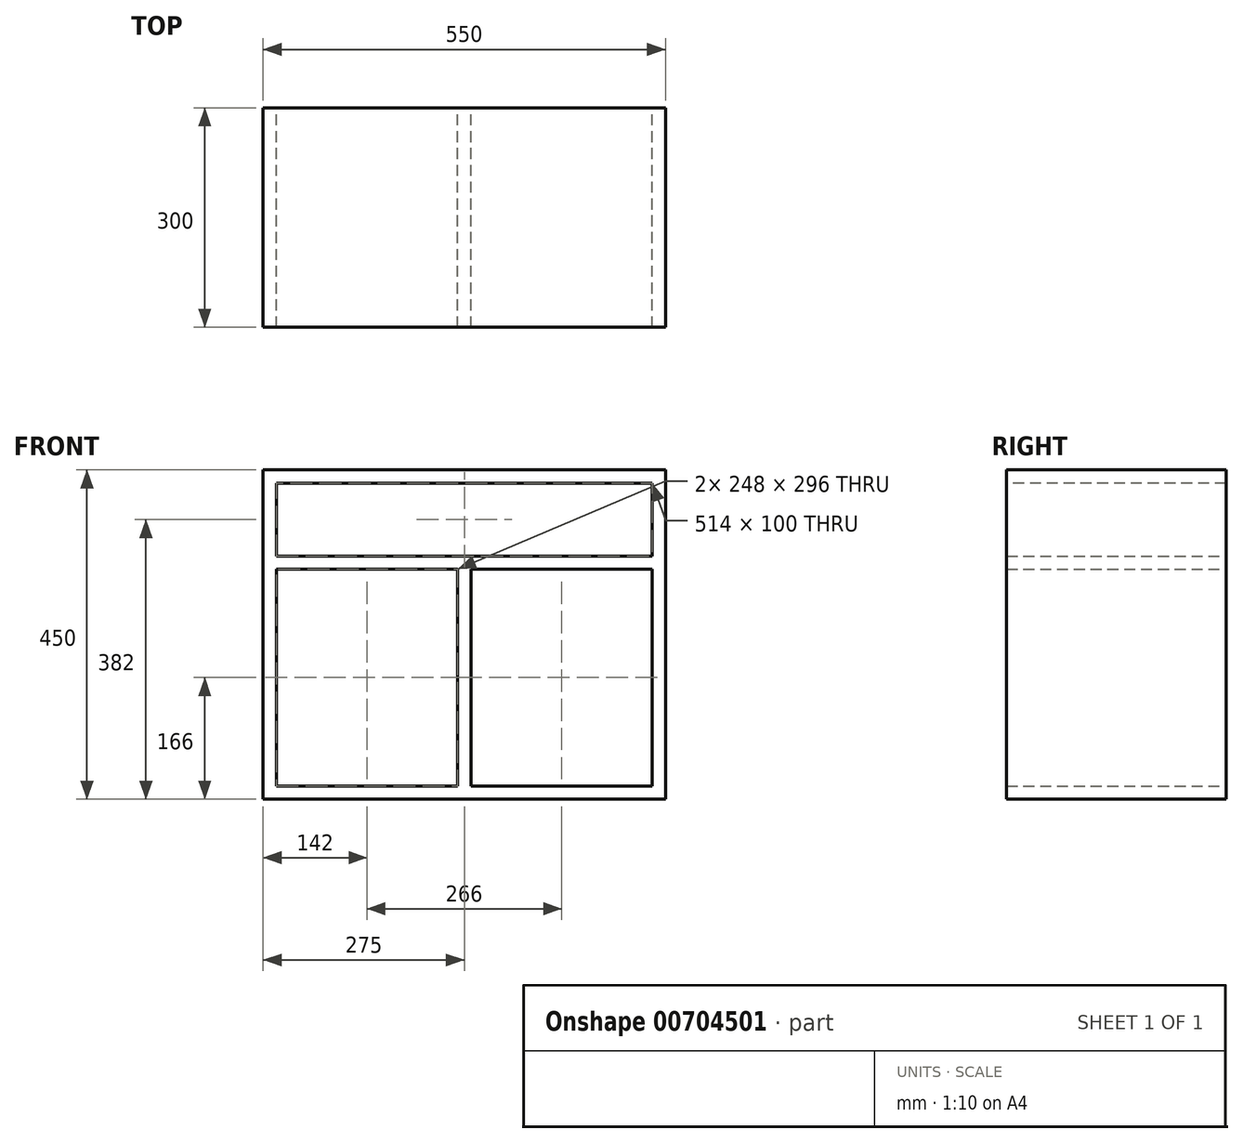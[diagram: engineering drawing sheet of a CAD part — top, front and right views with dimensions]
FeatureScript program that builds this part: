
annotation { "Feature Type Name" : "Feature", "Feature Type Description" : "" }
export const myFeature = defineFeature(function(context is Context, id is Id, definition is map)
    precondition{}
    {
        {
            var Q0;
            Q0=qCreatedBy(makeId("Top.planeOp"),FACE);
            var sketch = newSketch(context, id + "F0", { "sketchPlane" : qUnion([Q0])});
            skLineSegment(sketch, "E0.bottom", {"start": v(275, -150) * mm, "end": v(-275, -150) * mm});
            skLineSegment(sketch, "E0.top", {"start": v(275, 150) * mm, "end": v(-275, 150) * mm});
            skLineSegment(sketch, "E0.left", {"start": v(275, -150) * mm, "end": v(275, 150) * mm});
            skLineSegment(sketch, "E0.right", {"start": v(-275, -150) * mm, "end": v(-275, 150) * mm});
            skPoint(sketch, "E0.middle", {"position": v(0, 0) * mm});
            skSolve(sketch);
        }
        {
            var Q0;
            Q0=makeQuery(id+"F0.imprint","IMPRINT",FACE,{"disambiguationData":[TD([[makeQuery(id+"F0.imprint","IMPRINT",EDGE,{"derivedFrom":sQuery(id+"F0.wireOp",EDGE,"E0.bottom")}),-1.0]])]});
            extrude(context, id + "F1", {"entities" : qUnion([Q0]), "depth" : 18 * mm, "offsetDistance" : 25 * mm});
        }
        {
            var Q0;
            Q0=makeQuery(id+"F1.opExtrude","CAP_FACE",FACE,{"disambiguationData":[OSD([sQuery(id+"F0.wireOp",EDGE,"E0.bottom"),sQuery(id+"F0.wireOp",EDGE,"E0.top"),sQuery(id+"F0.wireOp",EDGE,"E0.left"),sQuery(id+"F0.wireOp",EDGE,"E0.right")])],"isStart":false});
            var sketch = newSketch(context, id + "F2", { "sketchPlane" : qUnion([Q0])});
            skLineSegment(sketch, "E1.bottom", {"start": v(-275, 150) * mm, "end": v(-257, 150) * mm});
            skLineSegment(sketch, "E1.top", {"start": v(-275, -150) * mm, "end": v(-257, -150) * mm});
            skLineSegment(sketch, "E1.left", {"start": v(-275, 150) * mm, "end": v(-275, -150) * mm});
            skLineSegment(sketch, "E1.right", {"start": v(-257, 150) * mm, "end": v(-257, -150) * mm});
            skLineSegment(sketch, "E2.bottom", {"start": v(257, 150) * mm, "end": v(275, 150) * mm});
            skLineSegment(sketch, "E2.top", {"start": v(257, -150) * mm, "end": v(275, -150) * mm});
            skLineSegment(sketch, "E2.left", {"start": v(257, 150) * mm, "end": v(257, -150) * mm});
            skLineSegment(sketch, "E2.right", {"start": v(275, 150) * mm, "end": v(275, -150) * mm});
            skSolve(sketch);
        }
        {
            var Q0;
            Q0 = qSketchRegion(id + "F2", true);
            extrude(context, id + "F3", {"entities" : qUnion([Q0]), "operationType" : NewBodyOperationType.ADD, "depth" : 414 * mm, "offsetDistance" : 25 * mm});
        }
        {
            var Q0;
            Q0=makeQuery(id+"F1.opExtrude","CAP_FACE",FACE,{"disambiguationData":[OSD([sQuery(id+"F0.wireOp",EDGE,"E0.bottom"),sQuery(id+"F0.wireOp",EDGE,"E0.top"),sQuery(id+"F0.wireOp",EDGE,"E0.left"),sQuery(id+"F0.wireOp",EDGE,"E0.right")])],"isStart":false});
            var sketch = newSketch(context, id + "F4", { "sketchPlane" : qUnion([Q0])});
            skLineSegment(sketch, "E3.bottom", {"start": v(9, -150) * mm, "end": v(-9, -150) * mm});
            skLineSegment(sketch, "E3.top", {"start": v(9, 150) * mm, "end": v(-9, 150) * mm});
            skLineSegment(sketch, "E3.left", {"start": v(9, -150) * mm, "end": v(9, 150) * mm});
            skLineSegment(sketch, "E3.right", {"start": v(-9, -150) * mm, "end": v(-9, 150) * mm});
            skPoint(sketch, "E3.middle", {"position": v(0, 0) * mm});
            skSolve(sketch);
        }
        {
            var Q0;
            Q0 = qSketchRegion(id + "F4", true);
            extrude(context, id + "F5", {"entities" : qUnion([Q0]), "operationType" : NewBodyOperationType.ADD, "depth" : 296 * mm, "offsetDistance" : 25 * mm});
        }
        {
            var Q0;
            Q0=makeQuery(id+"F5.opExtrude","CAP_FACE",FACE,{"disambiguationData":[OSD([sQuery(id+"F4.wireOp",EDGE,"E3.bottom"),sQuery(id+"F4.wireOp",EDGE,"E3.top"),sQuery(id+"F4.wireOp",EDGE,"E3.left"),sQuery(id+"F4.wireOp",EDGE,"E3.right")])],"isStart":false});
            var sketch = newSketch(context, id + "F6", { "sketchPlane" : qUnion([Q0])});
            skLineSegment(sketch, "E4.bottom", {"start": v(257, -150) * mm, "end": v(-257, -150) * mm});
            skLineSegment(sketch, "E4.top", {"start": v(257, 150) * mm, "end": v(-257, 150) * mm});
            skLineSegment(sketch, "E4.left", {"start": v(257, -150) * mm, "end": v(257, 150) * mm});
            skLineSegment(sketch, "E4.right", {"start": v(-257, -150) * mm, "end": v(-257, 150) * mm});
            skPoint(sketch, "E4.middle", {"position": v(0, 0) * mm});
            skSolve(sketch);
        }
        {
            var Q0;
            {var subQ2=sQuery(id+"F6.wireOp",EDGE,"E4.left");Q0=makeQuery(id+"F6.imprint","IMPRINT",FACE,{"disambiguationData":[TD([[makeQuery(id+"F6.imprint","IMPRINT",EDGE,{"derivedFrom":subQ2}),1.0]])]});}
            var Q1;
            {var subQ1=makeQuery(id+"F5.opExtrude","CAP_EDGE",EDGE,{"disambiguationData":[OSD([sQuery(id+"F4.wireOp",EDGE,"E3.left")])],"isStart":false});Q1=makeQuery(id+"F6.imprint","IMPRINT",FACE,{"disambiguationData":[TD([[makeQuery(id+"F6.imprint","IMPRINT",EDGE,{"derivedFrom":subQ1}),1.0]])]});}
            var Q2;
            {var subQ2=sQuery(id+"F6.wireOp",EDGE,"E4.right");Q2=makeQuery(id+"F6.imprint","IMPRINT",FACE,{"disambiguationData":[TD([[makeQuery(id+"F6.imprint","IMPRINT",EDGE,{"derivedFrom":subQ2}),-1.0]])]});}
            extrude(context, id + "F7", {"entities" : qUnion([Q0, Q1, Q2]), "operationType" : NewBodyOperationType.ADD, "depth" : 18 * mm, "offsetDistance" : 25 * mm});
        }
        {
            var Q0;
            Q0=makeQuery(id+"F3.opExtrude","CAP_FACE",FACE,{"disambiguationData":[OSD([sQuery(id+"F2.wireOp",EDGE,"E1.bottom"),sQuery(id+"F2.wireOp",EDGE,"E1.top"),sQuery(id+"F2.wireOp",EDGE,"E1.left"),sQuery(id+"F2.wireOp",EDGE,"E1.right")])],"isStart":false});
            var sketch = newSketch(context, id + "F8", { "sketchPlane" : qUnion([Q0])});
            skLineSegment(sketch, "E5.bottom", {"start": v(275, -150) * mm, "end": v(-275, -150) * mm});
            skLineSegment(sketch, "E5.top", {"start": v(275, 150) * mm, "end": v(-275, 150) * mm});
            skLineSegment(sketch, "E5.left", {"start": v(275, -150) * mm, "end": v(275, 150) * mm});
            skLineSegment(sketch, "E5.right", {"start": v(-275, -150) * mm, "end": v(-275, 150) * mm});
            skPoint(sketch, "E5.middle", {"position": v(0, 0) * mm});
            skSolve(sketch);
        }
        {
            var Q0;
            {var subQ2=sQuery(id+"F8.wireOp",EDGE,"E5.left");Q0=makeQuery(id+"F8.imprint","IMPRINT",FACE,{"disambiguationData":[TD([[makeQuery(id+"F8.imprint","IMPRINT",EDGE,{"derivedFrom":subQ2}),1.0]])]});}
            var Q1;
            {var subQ0=sQuery(id+"F8.wireOp",EDGE,"E5.right");Q1=makeQuery(id+"F8.imprint","IMPRINT",FACE,{"disambiguationData":[TD([[makeQuery(id+"F8.imprint","IMPRINT",EDGE,{"derivedFrom":subQ0}),-1.0]])]});}
            extrude(context, id + "F9", {"entities" : qUnion([Q0, Q1]), "operationType" : NewBodyOperationType.ADD, "depth" : 18 * mm, "offsetDistance" : 25 * mm});
        }
    });
